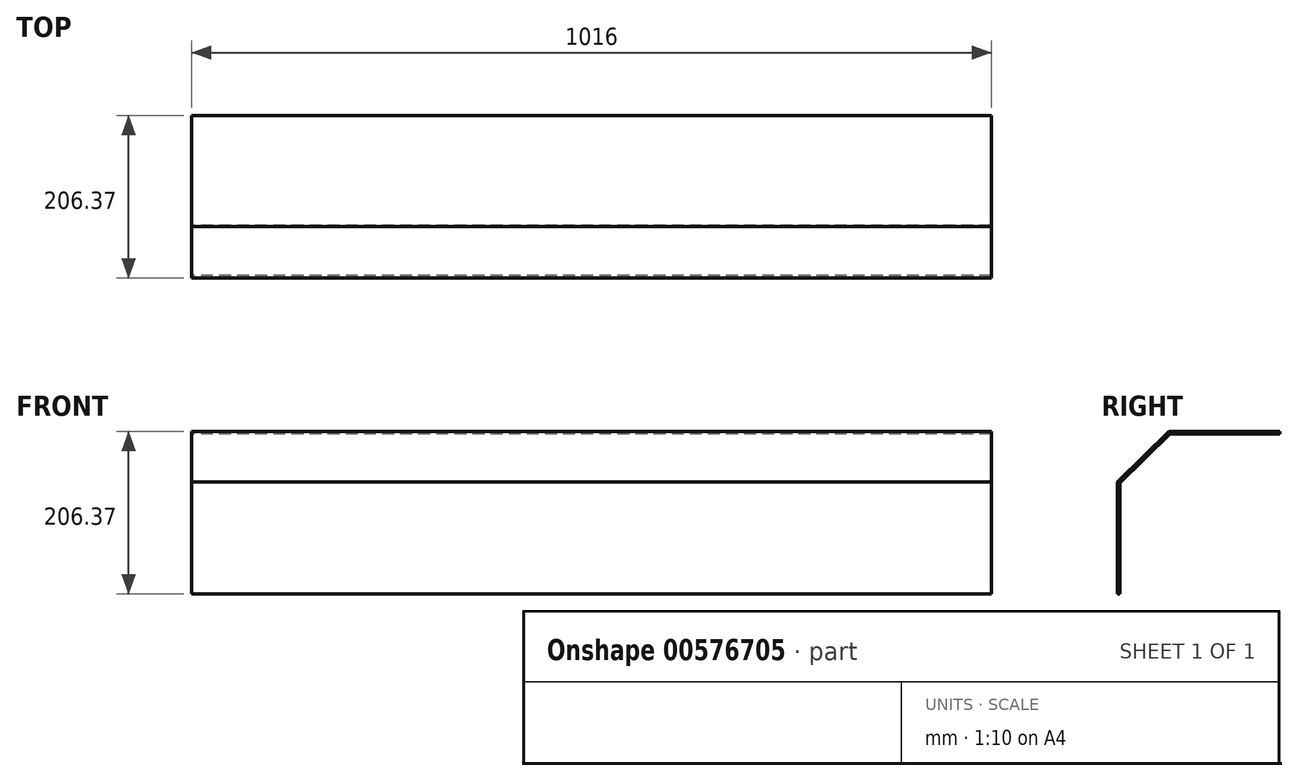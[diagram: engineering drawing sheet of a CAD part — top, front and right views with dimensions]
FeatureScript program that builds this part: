
annotation { "Feature Type Name" : "Feature", "Feature Type Description" : "" }
export const myFeature = defineFeature(function(context is Context, id is Id, definition is map)
    precondition{}
    {
        {
            var Q0;
            Q0=qCreatedBy(makeId("Right.planeOp"),FACE);
            var sketch = newSketch(context, id + "F0", { "sketchPlane" : qUnion([Q0])});
            skLineSegment(sketch, "E0.bottom", {"start": v(101.6, 101.6) * mm, "end": v(-38.1, 101.6) * mm});
            skLineSegment(sketch, "E0.right", {"start": v(-101.6, 39.38) * mm, "end": v(-101.6, -101.6) * mm});
            skPoint(sketch, "E0.middle", {"position": v(0, 0) * mm});
            skLineSegment(sketch, "E1", {"start": v(-38.1, 101.6) * mm, "end": v(-101.6, 39.38) * mm});
            skPoint(sketch, "E2.orphan", {"position": v(-101.6, 101.6) * mm});
            skLineSegment(sketch, "E3.0", {"start": v(-104.77, 40.71) * mm, "end": v(-104.78, -101.6) * mm});
            skLineSegment(sketch, "E3.1", {"start": v(-39.4, 104.78) * mm, "end": v(-104.77, 40.71) * mm});
            skLineSegment(sketch, "E3.2", {"start": v(101.6, 104.78) * mm, "end": v(-39.4, 104.78) * mm});
            skPoint(sketch, "E0.top.start.orphan", {"position": v(101.6, -101.6) * mm});
            skLineSegment(sketch, "E4", {"start": v(101.6, 104.78) * mm, "end": v(101.6, 101.6) * mm});
            skLineSegment(sketch, "E5", {"start": v(-104.78, -101.6) * mm, "end": v(-101.6, -101.6) * mm});
            skSolve(sketch);
        }
        {
            var Q0;
            Q0=makeQuery(id+"F0.imprint","IMPRINT",FACE,{"disambiguationData":[TD([[makeQuery(id+"F0.imprint","IMPRINT",EDGE,{"derivedFrom":sQuery(id+"F0.wireOp",EDGE,"E0.bottom")}),-1.0]])]});
            extrude(context, id + "F1", {"entities" : qUnion([Q0]), "depth" : 1016 * mm, "offsetDistance" : 25.4 * mm});
        }
    });
